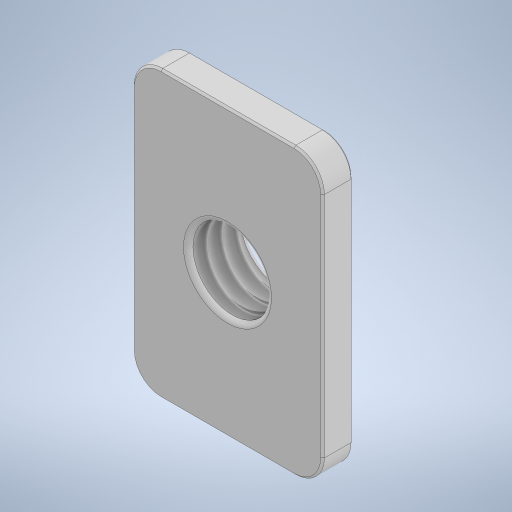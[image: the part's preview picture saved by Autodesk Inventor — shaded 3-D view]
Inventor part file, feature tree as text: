
AUTODESK INVENTOR PART (.ipt)
format: ipt  version: 2024 (Build 280153000, 153)  size: 285,696 bytes
history: native  units: mm
features: fillet x3, sketch x3, extrude x2, chamfer x2, hole x1
ambient origin geometry x8: Origin, YZ Plane, XZ Plane, XY Plane, X Axis, Y Axis, Z Axis, Center Point
bodies: Solid1 (feature_tree)
feature tree (11):
  extrude  "Extrusion1"  Depth=15.0mm
  extrude  "Extrusion2"  Depth=0.25mm
  fillet  "Fillet1"  Radius=1.4mm
  fillet  "Fillet2"  Radius=0.25mm
  hole  "Hole1"  [1 undecoded]
  fillet  "Fillet3"  Radius=0.1mm
  chamfer  "Chamfer1"  Distance=0.1mm Angle=45.0deg
  chamfer  "Chamfer2"  [1 undecoded]
  sketch  "Sketch1"  dims[d0=10.0mm d1=15.0mm]
  sketch  "Sketch2"  dims[d2=1.6mm d3=0.0mm d4=6.9mm d5=1.4mm d6=0.0mm d7=0.25mm]
  sketch  "Sketch3"  dims[d8=1.5mm d9=4.134mm d10=10.0mm d11=4.0mm d12=2.0mm d13=90.0deg d14=14.2mm d15=150.0deg d16=0.25mm d17=0.1mm d18=2.0mm d19=45.0deg d20=0.1mm d21=2.0mm d22=45.0deg]
note: 2 required parameter values undecoded (feature->parameter linkage not recoverable at this tier; creation-order binding heuristic only, values carry confidence <= 0.55)
